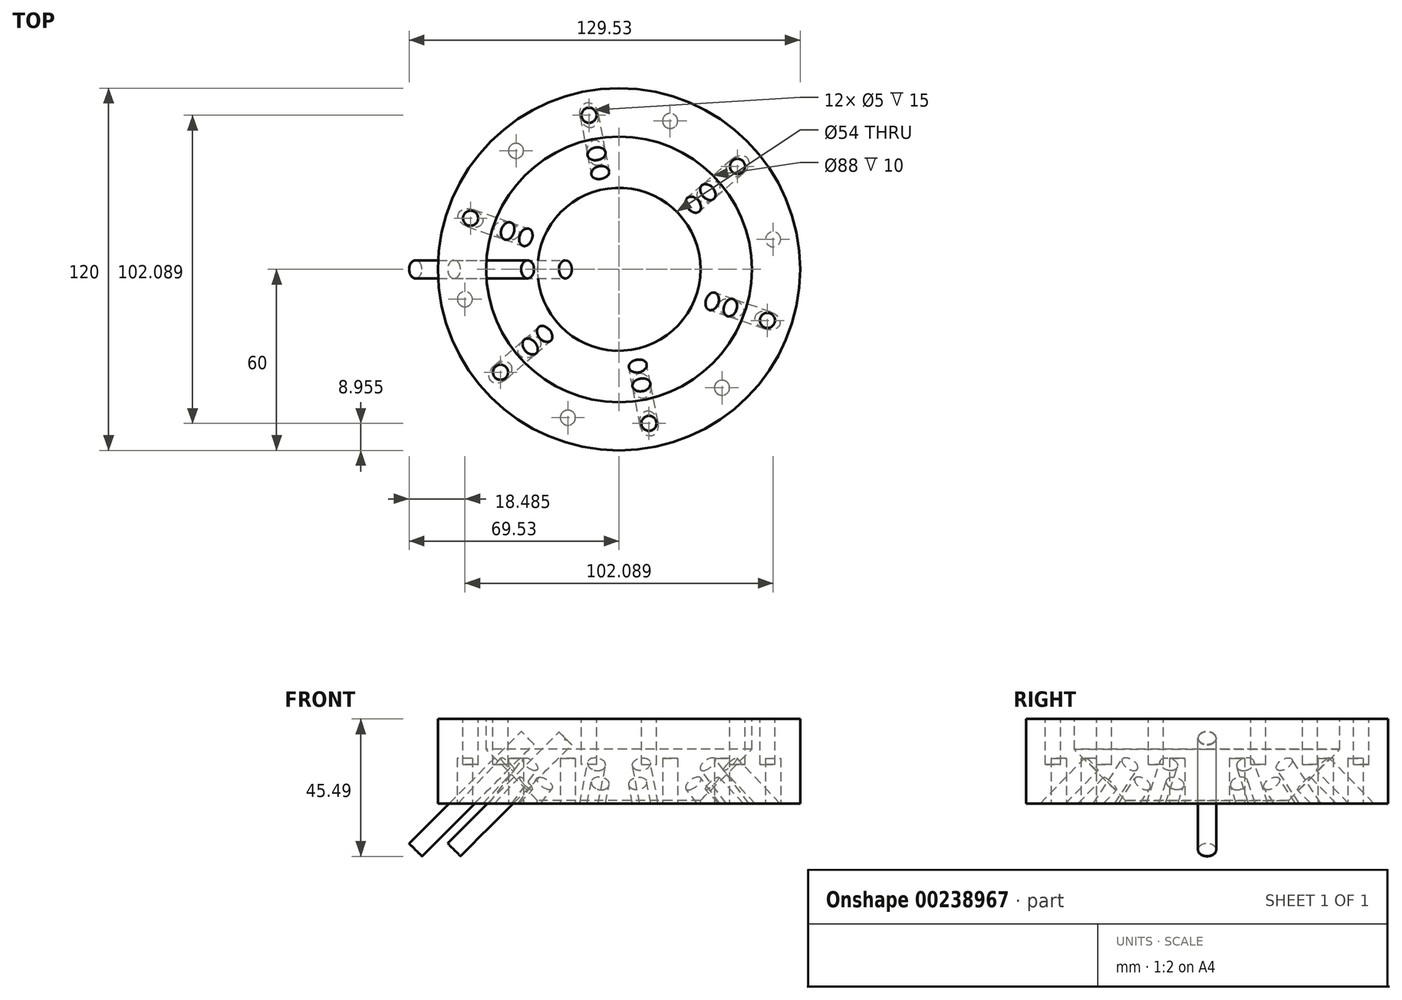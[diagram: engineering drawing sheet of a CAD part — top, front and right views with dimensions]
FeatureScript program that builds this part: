
annotation { "Feature Type Name" : "Feature", "Feature Type Description" : "" }
export const myFeature = defineFeature(function(context is Context, id is Id, definition is map)
    precondition{}
    {
        {
            var Q0;
            Q0=qCreatedBy(makeId("Front.planeOp"),FACE);
            var sketch = newSketch(context, id + "F0", { "sketchPlane" : qUnion([Q0])});
            skLineSegment(sketch, "E0", {"start": v(0, 70.12) * mm, "end": v(0, -51.14) * mm, "construction": true});
            skLineSegment(sketch, "E1", {"start": v(-40, -25.13) * mm, "end": v(-40, -82.12) * mm, "construction": true});
            skLineSegment(sketch, "E2", {"start": v(-33.5, -13) * mm, "end": v(-33.5, -83.09) * mm, "construction": true});
            skLineSegment(sketch, "E3", {"start": v(-55, -23.79) * mm, "end": v(-55, -71.7) * mm, "construction": true});
            skPoint(sketch, "E4", {"position": v(-45, -20) * mm});
            skLineSegment(sketch, "E5", {"start": v(-27, -2) * mm, "end": v(-44, 15) * mm});
            skLineSegment(sketch, "E6", {"start": v(-44, 20) * mm, "end": v(0, 20) * mm, "construction": true});
            skLineSegment(sketch, "E7.trimOffspring", {"start": v(-44, 15) * mm, "end": v(-44, 25) * mm});
            skLineSegment(sketch, "E8", {"start": v(0, 20) * mm, "end": v(0, -2) * mm});
            skLineSegment(sketch, "E9", {"start": v(-15, -3) * mm, "end": v(-15, -14) * mm});
            skLineSegment(sketch, "E10.trimOffspring", {"start": v(-44, 25) * mm, "end": v(-60, 25) * mm});
            skLineSegment(sketch, "E11", {"start": v(-27, -14) * mm, "end": v(-60, -14) * mm, "construction": true});
            skLineSegment(sketch, "E12", {"start": v(-44, -3) * mm, "end": v(-26, -3) * mm});
            skLineSegment(sketch, "E13", {"start": v(-60.56, -2) * mm, "end": v(-7.47, -2) * mm, "construction": true});
            skLineSegment(sketch, "E14", {"start": v(-32.2, -0.13) * mm, "end": v(-20.33, 11.74) * mm, "construction": true});
            skLineSegment(sketch, "E15", {"start": v(-37.48, 3.07) * mm, "end": v(-25.45, 15.1) * mm, "construction": true});
            skLineSegment(sketch, "E16", {"start": v(-39.45, 6.77) * mm, "end": v(-29.58, 16.63) * mm, "construction": true});
            skLineSegment(sketch, "E17", {"start": v(-44.65, 10.05) * mm, "end": v(-35.06, 19.64) * mm, "construction": true});
            skPoint(sketch, "E18", {"position": v(-27, -2) * mm});
            skLineSegment(sketch, "E19", {"start": v(-27, -2) * mm, "end": v(-16.61, 8.39) * mm, "construction": true});
            skLineSegment(sketch, "E20", {"start": v(-60, 25) * mm, "end": v(-60, -3) * mm});
            skLineSegment(sketch, "E21", {"start": v(-27, -2) * mm, "end": v(-27, -3) * mm});
            skLineSegment(sketch, "E22", {"start": v(-44, -3) * mm, "end": v(-44, -3) * mm});
            skLineSegment(sketch, "E23", {"start": v(-67.6, -3) * mm, "end": v(-41.15, -3) * mm});
            skSolve(sketch);
        }
        {
            var Q0;
            Q0=makeQuery(id+"F0.imprint","IMPRINT",FACE,{"disambiguationData":[TD([[makeQuery(id+"F0.imprint","IMPRINT",EDGE,{"derivedFrom":sQuery(id+"F0.wireOp",EDGE,"E5")}),1.0]])]});
            var Q1;
            Q1=sQuery(id+"F0.wireOp",EDGE,"E8");
            revolve(context, id + "F1", {"entities" : qUnion([Q0]), "axis" : qUnion([Q1]), "revolveType" : RevolveType.FULL});
        }
        {
            var Q0;
            Q0=qCreatedBy(makeId("Front.planeOp"),FACE);
            var sketch = newSketch(context, id + "F2", { "sketchPlane" : qUnion([Q0])});
            skLineSegment(sketch, "E24.0", {"start": v(-55, -23.79) * mm, "end": v(-55, -71.7) * mm, "construction": true});
            skLineSegment(sketch, "E25.0", {"start": v(-33.5, -13) * mm, "end": v(-33.5, -83.09) * mm, "construction": true});
            skLineSegment(sketch, "E26", {"start": v(-30.26, 18.78) * mm, "end": v(-67.4, -18.36) * mm});
            skLineSegment(sketch, "E27", {"start": v(-32.38, 20.9) * mm, "end": v(-30.26, 18.78) * mm});
            skLineSegment(sketch, "E28", {"start": v(-69.53, -16.24) * mm, "end": v(-67.4, -18.36) * mm});
            skLineSegment(sketch, "E29.0", {"start": v(-27, -2) * mm, "end": v(-44, 15) * mm});
            skLineSegment(sketch, "E30.0", {"start": v(-27, -2) * mm, "end": v(-16.61, 8.39) * mm, "construction": true});
            skLineSegment(sketch, "E31", {"start": v(-32.38, 20.9) * mm, "end": v(-69.53, -16.24) * mm});
            skPoint(sketch, "E32", {"position": v(0, 0) * mm});
            skSolve(sketch);
        }
        {
            var Q0;
            Q0=qSketchRegion(id+"F2",true);
            var Q1;
            Q1=sQuery(id+"F2.wireOp",EDGE,"E26");
            revolve(context, id + "F3", {"entities" : qUnion([Q0]), "axis" : qUnion([Q1]), "revolveType" : RevolveType.FULL});
        }
        {
            var Q0;
            Q0=makeQuery(id+"F3.opRevolve","SWEPT_BODY",BODY,{"disambiguationData":[OSD([sQuery(id+"F2.wireOp",EDGE,"8dca1c6b-01d1-403d-97e6-a70b6a6dedc9.0"),sQuery(id+"F2.wireOp",EDGE,"E26"),sQuery(id+"F2.wireOp",EDGE,"E27"),sQuery(id+"F2.wireOp",EDGE,"BTjxJDAI-CfnJ-hfkt-lCJ7-kgF73TjLmZTi")])]});
            var Q1;
            Q1=sQuery(id+"F0.wireOp",EDGE,"E0");
            circularPattern(context, id + "F4", {"entities" : qUnion([Q0]), "axis" : qUnion([Q1]), "angle" : 19 * degree, "instanceCount" : 2, "equalSpace" : true});
        }
        {
            var Q0;
            Q0=makeQuery(id+"F4.opPattern","COPY",BODY,{"derivedFrom":makeQuery(id+"F3.opRevolve","SWEPT_BODY",BODY,{"disambiguationData":[OSD([sQuery(id+"F2.wireOp",EDGE,"8dca1c6b-01d1-403d-97e6-a70b6a6dedc9.0"),sQuery(id+"F2.wireOp",EDGE,"E26"),sQuery(id+"F2.wireOp",EDGE,"E27"),sQuery(id+"F2.wireOp",EDGE,"BTjxJDAI-CfnJ-hfkt-lCJ7-kgF73TjLmZTi")])]}),"instanceName":"1"});
            var Q1;
            Q1=sQuery(id+"F0.wireOp",EDGE,"E0");
            circularPattern(context, id + "F5", {"operationType" : NewBodyOperationType.REMOVE, "entities" : qUnion([Q0]), "axis" : qUnion([Q1]), "angle" : 360 * degree, "instanceCount" : 6, "equalSpace" : true});
        }
        {
            var Q0;
            Q0=qCreatedBy(makeId("Front.planeOp"),FACE);
            var sketch = newSketch(context, id + "F6", { "sketchPlane" : qUnion([Q0])});
            skLineSegment(sketch, "E33.0", {"start": v(-27, -2) * mm, "end": v(-44, 15) * mm, "construction": true});
            skLineSegment(sketch, "E34", {"start": v(-17.75, 18.57) * mm, "end": v(-54.69, -18.37) * mm});
            skLineSegment(sketch, "E35", {"start": v(-19.87, 20.69) * mm, "end": v(-17.75, 18.57) * mm});
            skLineSegment(sketch, "E36", {"start": v(-56.75, -16.2) * mm, "end": v(-54.63, -18.31) * mm});
            skLineSegment(sketch, "E37", {"start": v(-19.87, 20.69) * mm, "end": v(-56.75, -16.2) * mm});
            skSolve(sketch);
        }
        {
            var Q0;
            Q0=qSketchRegion(id+"F6",true);
            var Q1;
            Q1=sQuery(id+"F6.wireOp",EDGE,"E33.0");
            var Q2;
            Q2=sQuery(id+"F6.wireOp",EDGE,"E34");
            revolve(context, id + "F7", {"entities" : qUnion([Q0]), "surfaceEntities" : qUnion([Q1]), "axis" : qUnion([Q2]), "revolveType" : RevolveType.FULL});
        }
        {
            var Q0;
            Q0=makeQuery(id+"F7.opRevolve","SWEPT_BODY",BODY,{"disambiguationData":[OSD([sQuery(id+"F6.wireOp",EDGE,"0296a30f-b775-46fb-957b-19e912f0fa4b.0"),sQuery(id+"F6.wireOp",EDGE,"E34"),sQuery(id+"F6.wireOp",EDGE,"E35"),sQuery(id+"F6.wireOp",EDGE,"E36")])]});
            var Q1;
            Q1=sQuery(id+"F0.wireOp",EDGE,"E0");
            circularPattern(context, id + "F8", {"entities" : qUnion([Q0]), "axis" : qUnion([Q1]), "angle" : 19 * degree, "instanceCount" : 2, "equalSpace" : true});
        }
        {
            var Q0;
            Q0=makeQuery(id+"F8.opPattern","COPY",BODY,{"derivedFrom":makeQuery(id+"F7.opRevolve","SWEPT_BODY",BODY,{"disambiguationData":[OSD([sQuery(id+"F6.wireOp",EDGE,"0296a30f-b775-46fb-957b-19e912f0fa4b.0"),sQuery(id+"F6.wireOp",EDGE,"E34"),sQuery(id+"F6.wireOp",EDGE,"E35"),sQuery(id+"F6.wireOp",EDGE,"E36")])]}),"instanceName":"1"});
            var Q1;
            Q1=makeQuery(id+"F1.opRevolve","SWEPT_FACE",FACE,{"disambiguationData":[OSD([sQuery(id+"F0.wireOp",EDGE,"E5")])]});
            circularPattern(context, id + "F9", {"operationType" : NewBodyOperationType.REMOVE, "entities" : qUnion([Q0]), "axis" : qUnion([Q1]), "angle" : 360 * degree, "instanceCount" : 6, "equalSpace" : true});
        }
        {
            var Q0;
            Q0=makeQuery(id+"F1.opRevolve","SWEPT_FACE",FACE,{"disambiguationData":[OSD([sQuery(id+"F0.wireOp",EDGE,"E12"),sQuery(id+"F0.wireOp",EDGE,"E23")])]});
            cPlane(context, id + "F10", {"entities" : qUnion([Q0]), "cplaneType" : CPlaneType.OFFSET, "offset" : 0 * mm, "width" : 150 * mm, "height" : 150 * mm});
        }
        {
            var Q0;
            Q0=qCreatedBy(id+"F10.planeOp",FACE);
            var sketch = newSketch(context, id + "F11", { "sketchPlane" : qUnion([Q0])});
            skLineSegment(sketch, "E38", {"start": v(70.55, -13.71) * mm, "end": v(0, 0) * mm, "construction": true});
            skCircle(sketch, "E39", {"center": v(0, 0) * mm, "radius": 52 * mm, "construction": true});
            skCircle(sketch, "E40", {"center": v(51.04, -9.92) * mm, "radius": 2.5 * mm});
            skSolve(sketch);
        }
        {
            var Q0;
            Q0=qSketchRegion(id+"F11",true);
            extrude(context, id + "F12", {"entities" : qUnion([Q0]), "oppositeDirection" : true, "depth" : 15 * mm, "hasSecondDirection" : true, "secondDirectionOppositeDirection" : false, "secondDirectionDepth" : 20 * mm});
        }
        {
            var Q0;
            Q0=makeQuery(id+"F12.opExtrude","SWEPT_BODY",BODY,{"disambiguationData":[OSD([sQuery(id+"F11.wireOp",EDGE,"E40")])]});
            var Q1;
            Q1=sQuery(id+"F0.wireOp",EDGE,"E8");
            circularPattern(context, id + "F13", {"operationType" : NewBodyOperationType.REMOVE, "entities" : qUnion([Q0]), "axis" : qUnion([Q1]), "angle" : 360 * degree, "instanceCount" : 6, "oppositeDirection" : true, "equalSpace" : true});
        }
        {
            var Q0;
            Q0=makeQuery(id+"F1.opRevolve","SWEPT_FACE",FACE,{"disambiguationData":[OSD([sQuery(id+"F0.wireOp",EDGE,"E10.trimOffspring")])]});
            cPlane(context, id + "F14", {"entities" : qUnion([Q0]), "cplaneType" : CPlaneType.OFFSET, "offset" : 0 * mm, "width" : 150 * mm, "height" : 150 * mm});
        }
        {
            var Q0;
            Q0=qCreatedBy(id+"F14.planeOp",FACE);
            var sketch = newSketch(context, id + "F15", { "sketchPlane" : qUnion([Q0])});
            skLineSegment(sketch, "E41", {"start": v(0, 0) * mm, "end": v(-15.23, 78.37) * mm, "construction": true});
            skCircle(sketch, "E42", {"center": v(0, 0) * mm, "radius": 52 * mm, "construction": true});
            skCircle(sketch, "E43", {"center": v(-9.92, 51.04) * mm, "radius": 2.5 * mm});
            skSolve(sketch);
        }
        {
            var Q0;
            Q0=qSketchRegion(id+"F15",true);
            extrude(context, id + "F16", {"entities" : qUnion([Q0]), "oppositeDirection" : true, "depth" : 15 * mm, "hasSecondDirection" : true, "secondDirectionOppositeDirection" : false, "secondDirectionDepth" : 20 * mm});
        }
        {
            var Q0;
            Q0=makeQuery(id+"F16.opExtrude","SWEPT_BODY",BODY,{"disambiguationData":[OSD([sQuery(id+"F15.wireOp",EDGE,"E43")])]});
            var Q1;
            Q1=sQuery(id+"F0.wireOp",EDGE,"E0");
            circularPattern(context, id + "F17", {"operationType" : NewBodyOperationType.REMOVE, "entities" : qUnion([Q0]), "axis" : qUnion([Q1]), "angle" : 360 * degree, "instanceCount" : 6, "equalSpace" : true});
        }
    });
